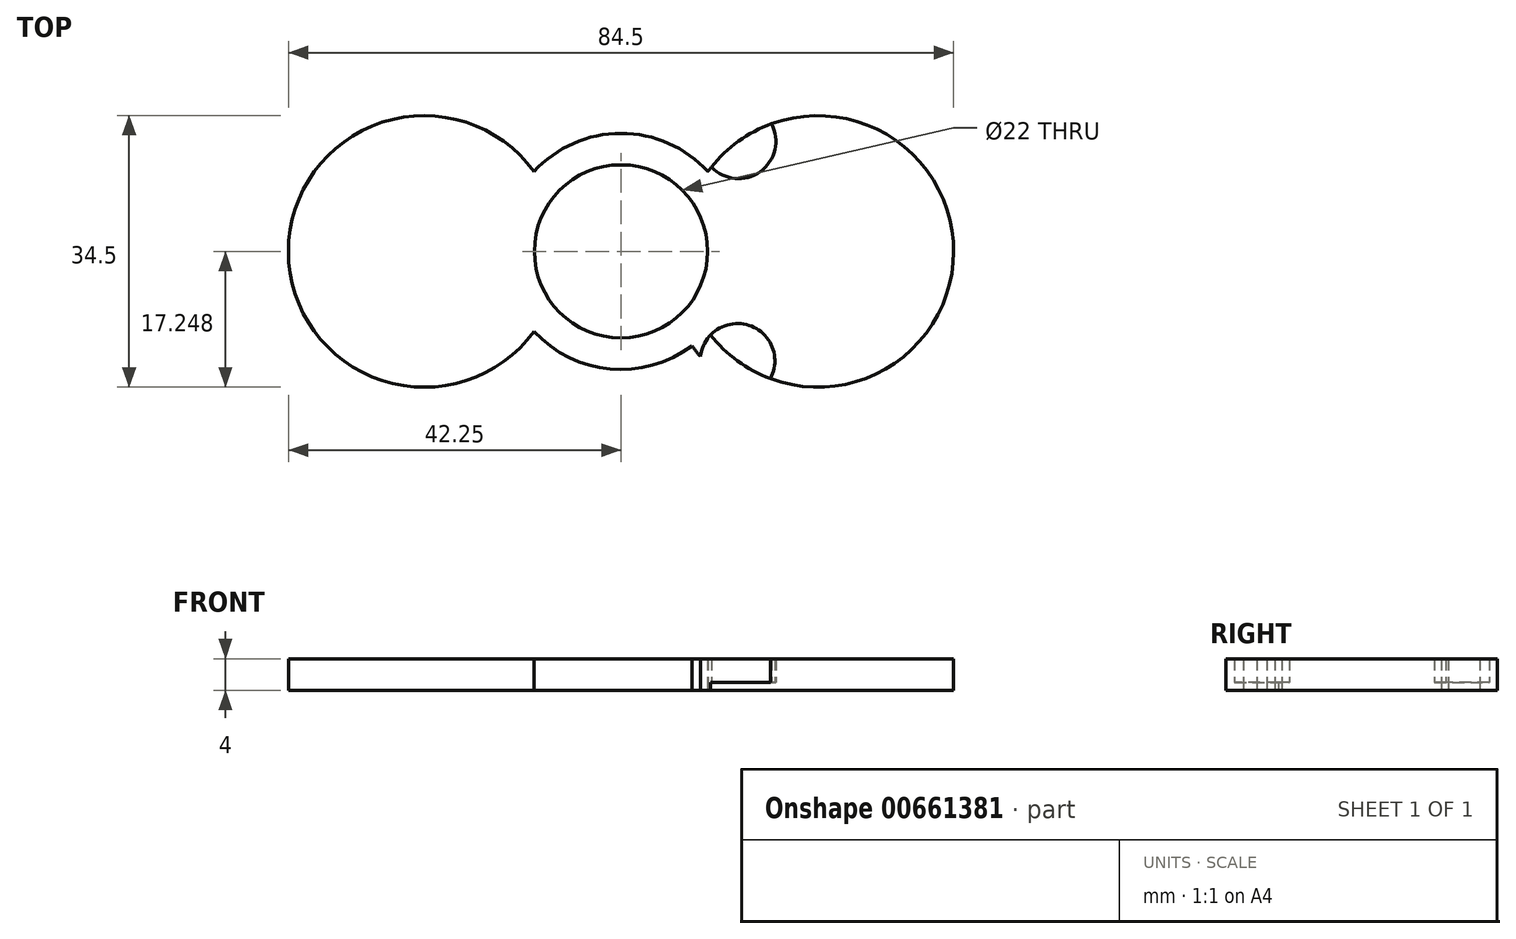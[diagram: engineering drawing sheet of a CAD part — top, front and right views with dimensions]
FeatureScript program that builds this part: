
annotation { "Feature Type Name" : "Feature", "Feature Type Description" : "" }
export const myFeature = defineFeature(function(context is Context, id is Id, definition is map)
    precondition{}
    {
        {
            var Q0;
            Q0=qCreatedBy(makeId("Top.planeOp"),FACE);
            var sketch = newSketch(context, id + "F0", { "sketchPlane" : qUnion([Q0])});
            skCircle(sketch, "E0", {"center": v(25, 38.23) * mm, "radius": 11 * mm});
            skCircle(sketch, "E1", {"center": v(25, 38.23) * mm, "radius": 15 * mm});
            skArc(sketch, "E2", {"start": v(16, 26.23) * mm, "mid": v(-11.02, 54.92) * mm, "end": v(4.76, 18.8) * mm});
            skArc(sketch, "E3", {"start": v(4.5, 57.72) * mm, "mid": v(25, 54.23) * mm, "end": v(45.5, 57.72) * mm});
            skPoint(sketch, "E4", {"position": v(4.5, 18.74) * mm});
            skPoint(sketch, "E5", {"position": v(45.5, 18.74) * mm});
            skArc(sketch, "E6", {"start": v(45.5, 18.74) * mm, "mid": v(40.9, 20.15) * mm, "end": v(36.2, 21.2) * mm});
            skCircle(sketch, "E7", {"center": v(0, 38.23) * mm, "radius": 17.25 * mm});
            skLineSegment(sketch, "E8.anchor1", {"start": v(0, 38.23) * mm, "end": v(0, 23.73) * mm, "construction": true});
            skPoint(sketch, "E9", {"position": v(50, 38.23) * mm});
            skCircle(sketch, "E10", {"center": v(50, 38.23) * mm, "radius": 20 * mm});
            skCircle(sketch, "E11", {"center": v(50, 38.23) * mm, "radius": 17.25 * mm});
            skCircle(sketch, "E12", {"center": v(0, 38.23) * mm, "radius": 7.75 * mm});
            skLineSegment(sketch, "E13", {"start": v(0, 38.23) * mm, "end": v(0, 45.98) * mm});
            skLineSegment(sketch, "E14", {"start": v(0, 45.98) * mm, "end": v(0, 50.73) * mm});
            skLineSegment(sketch, "E15.anchor1", {"start": v(0, 38.23) * mm, "end": v(0, 50.73) * mm, "construction": true});
            skLineSegment(sketch, "E15.anchor2", {"start": v(0, 38.23) * mm, "end": v(0, 25.73) * mm, "construction": true});
            skCircle(sketch, "E16", {"center": v(50, 38.23) * mm, "radius": 7.75 * mm});
            skLineSegment(sketch, "E17", {"start": v(50, 38.23) * mm, "end": v(50, 45.98) * mm});
            skLineSegment(sketch, "E18", {"start": v(50, 45.98) * mm, "end": v(50, 50.73) * mm});
            skCircle(sketch, "E19.1.0", {"center": v(39.92, 52.23) * mm, "radius": 4.75 * mm});
            skCircle(sketch, "E19.4.0", {"center": v(39.8, 24.32) * mm, "radius": 4.75 * mm});
            skLineSegment(sketch, "E19.anchor1", {"start": v(50, 38.23) * mm, "end": v(50, 50.73) * mm, "construction": true});
            skLineSegment(sketch, "E19.anchor2", {"start": v(50, 38.23) * mm, "end": v(50, 25.73) * mm, "construction": true});
            skPoint(sketch, "E20", {"position": v(4.76, 18.8) * mm});
            skSolve(sketch);
        }
        {
            var Q0;
            {var subQ1=sQuery(id+"F0.wireOp",EDGE,"E2");var subQ6=sQuery(id+"F0.wireOp",EDGE,"E1");var subQ7=makeQuery(id+"F0.imprint","INTERSECT",VERTEX,{"disambiguationData":[OD(0.0)],"derivedFrom":[subQ6,subQ1]});Q0=makeQuery(id+"F0.imprint","IMPRINT",FACE,{"disambiguationData":[TD([[makeQuery(id+"F0.imprint","IMPRINT",EDGE,{"disambiguationData":[TD([[subQ7,-1.0]])],"derivedFrom":subQ6}),-1.0]])]});}
            var Q1;
            {var subQ0=sQuery(id+"F0.wireOp",EDGE,"E12");var subQ1=makeQuery(id+"F0.imprint","IMPRINT",VERTEX,{"derivedFrom":subQ0});Q1=makeQuery(id+"F0.imprint","IMPRINT",FACE,{"disambiguationData":[TD([[makeQuery(id+"F0.imprint","IMPRINT",EDGE,{"disambiguationData":[TD([[subQ1,1.0]])],"derivedFrom":subQ0}),1.0]])]});}
            var Q2;
            {var subQ5=sQuery(id+"F0.wireOp",EDGE,"E7");var subQ6=sQuery(id+"F0.wireOp",EDGE,"E1");var subQ9=makeQuery(id+"F0.imprint","INTERSECT",VERTEX,{"disambiguationData":[OD(0.0)],"derivedFrom":[subQ6,subQ5]});Q2=makeQuery(id+"F0.imprint","IMPRINT",FACE,{"disambiguationData":[TD([[makeQuery(id+"F0.imprint","IMPRINT",EDGE,{"disambiguationData":[TD([[subQ9,-1.0]])],"derivedFrom":subQ6}),-1.0]])]});}
            var Q3;
            {var subQ0=sQuery(id+"F0.wireOp",EDGE,"E7");var subQ1=sQuery(id+"F0.wireOp",EDGE,"E0");var subQ2=makeQuery(id+"F0.imprint","INTERSECT",VERTEX,{"disambiguationData":[OD(0.0)],"derivedFrom":[subQ1,subQ0]});Q3=makeQuery(id+"F0.imprint","IMPRINT",FACE,{"disambiguationData":[TD([[makeQuery(id+"F0.imprint","IMPRINT",EDGE,{"disambiguationData":[TD([[subQ2,-1.0]])],"derivedFrom":subQ1}),-1.0]])]});}
            var Q4;
            {var subQ0=sQuery(id+"F0.wireOp",EDGE,"E2");var subQ1=sQuery(id+"F0.wireOp",EDGE,"E0");var subQ2=makeQuery(id+"F0.imprint","INTERSECT",VERTEX,{"disambiguationData":[OD(0.0)],"derivedFrom":[subQ1,subQ0]});Q4=makeQuery(id+"F0.imprint","IMPRINT",FACE,{"disambiguationData":[TD([[makeQuery(id+"F0.imprint","IMPRINT",EDGE,{"disambiguationData":[TD([[subQ2,-1.0]])],"derivedFrom":subQ1}),-1.0]])]});}
            var Q5;
            {var subQ0=sQuery(id+"F0.wireOp",EDGE,"E10");var subQ1=sQuery(id+"F0.wireOp",EDGE,"E0");var subQ2=makeQuery(id+"F0.imprint","INTERSECT",VERTEX,{"disambiguationData":[OD(0.0)],"derivedFrom":[subQ1,subQ0]});Q5=makeQuery(id+"F0.imprint","IMPRINT",FACE,{"disambiguationData":[TD([[makeQuery(id+"F0.imprint","IMPRINT",EDGE,{"disambiguationData":[TD([[subQ2,-1.0]])],"derivedFrom":subQ1}),-1.0]])]});}
            var Q6;
            {var subQ0=sQuery(id+"F0.wireOp",EDGE,"E10");var subQ1=sQuery(id+"F0.wireOp",EDGE,"E0");var subQ2=makeQuery(id+"F0.imprint","INTERSECT",VERTEX,{"disambiguationData":[OD(0.0)],"derivedFrom":[subQ1,subQ0]});Q6=makeQuery(id+"F0.imprint","IMPRINT",FACE,{"disambiguationData":[TD([[makeQuery(id+"F0.imprint","IMPRINT",EDGE,{"disambiguationData":[TD([[subQ2,1.0]])],"derivedFrom":subQ1}),-1.0]])]});}
            var Q7;
            {var subQ0=sQuery(id+"F0.wireOp",EDGE,"E11");var subQ1=sQuery(id+"F0.wireOp",EDGE,"E0");var subQ2=makeQuery(id+"F0.imprint","INTERSECT",VERTEX,{"disambiguationData":[OD(0.0)],"derivedFrom":[subQ1,subQ0]});Q7=makeQuery(id+"F0.imprint","IMPRINT",FACE,{"disambiguationData":[TD([[makeQuery(id+"F0.imprint","IMPRINT",EDGE,{"disambiguationData":[TD([[subQ2,1.0]])],"derivedFrom":subQ1}),-1.0]])]});}
            var Q8;
            {var subQ0=sQuery(id+"F0.wireOp",EDGE,"E10");var subQ1=sQuery(id+"F0.wireOp",EDGE,"E0");var subQ2=makeQuery(id+"F0.imprint","INTERSECT",VERTEX,{"disambiguationData":[OD(1.0)],"derivedFrom":[subQ1,subQ0]});Q8=makeQuery(id+"F0.imprint","IMPRINT",FACE,{"disambiguationData":[TD([[makeQuery(id+"F0.imprint","IMPRINT",EDGE,{"disambiguationData":[TD([[subQ2,-1.0]])],"derivedFrom":subQ1}),-1.0]])]});}
            var Q9;
            {var subQ0=sQuery(id+"F0.wireOp",EDGE,"E2");var subQ1=sQuery(id+"F0.wireOp",EDGE,"E0");var subQ2=makeQuery(id+"F0.imprint","INTERSECT",VERTEX,{"disambiguationData":[OD(1.0)],"derivedFrom":[subQ1,subQ0]});Q9=makeQuery(id+"F0.imprint","IMPRINT",FACE,{"disambiguationData":[TD([[makeQuery(id+"F0.imprint","IMPRINT",EDGE,{"disambiguationData":[TD([[subQ2,-1.0]])],"derivedFrom":subQ1}),-1.0]])]});}
            var Q10;
            {var subQ0=sQuery(id+"F0.wireOp",EDGE,"E2");var subQ1=sQuery(id+"F0.wireOp",EDGE,"E1");var subQ2=makeQuery(id+"F0.imprint","INTERSECT",VERTEX,{"disambiguationData":[OD(1.0)],"derivedFrom":[subQ1,subQ0]});Q10=makeQuery(id+"F0.imprint","IMPRINT",FACE,{"disambiguationData":[TD([[makeQuery(id+"F0.imprint","IMPRINT",EDGE,{"disambiguationData":[TD([[subQ2,-1.0]])],"derivedFrom":subQ1}),-1.0]])]});}
            var Q11;
            {var subQ0=sQuery(id+"F0.wireOp",EDGE,"E10");var subQ1=sQuery(id+"F0.wireOp",EDGE,"E1");var subQ2=makeQuery(id+"F0.imprint","INTERSECT",VERTEX,{"disambiguationData":[OD(0.0)],"derivedFrom":[subQ1,subQ0]});Q11=makeQuery(id+"F0.imprint","IMPRINT",FACE,{"disambiguationData":[TD([[makeQuery(id+"F0.imprint","IMPRINT",EDGE,{"disambiguationData":[TD([[subQ2,-1.0]])],"derivedFrom":subQ1}),-1.0]])]});}
            var Q12;
            {var subQ0=sQuery(id+"F0.wireOp",EDGE,"E7");var subQ1=sQuery(id+"F0.wireOp",EDGE,"E0");var subQ2=makeQuery(id+"F0.imprint","INTERSECT",VERTEX,{"disambiguationData":[OD(1.0)],"derivedFrom":[subQ1,subQ0]});Q12=makeQuery(id+"F0.imprint","IMPRINT",FACE,{"disambiguationData":[TD([[makeQuery(id+"F0.imprint","IMPRINT",EDGE,{"disambiguationData":[TD([[subQ2,-1.0]])],"derivedFrom":subQ1}),-1.0]])]});}
            var Q13;
            {var subQ0=sQuery(id+"F0.wireOp",EDGE,"E10");var subQ10=sQuery(id+"F0.wireOp",EDGE,"E1");var subQ11=makeQuery(id+"F0.imprint","INTERSECT",VERTEX,{"disambiguationData":[OD(0.0)],"derivedFrom":[subQ10,subQ0]});Q13=makeQuery(id+"F0.imprint","IMPRINT",FACE,{"disambiguationData":[TD([[makeQuery(id+"F0.imprint","IMPRINT",EDGE,{"disambiguationData":[TD([[subQ11,1.0]])],"derivedFrom":subQ10}),-1.0]])]});}
            var Q14;
            {var subQ5=sQuery(id+"F0.wireOp",EDGE,"E11");var subQ6=sQuery(id+"F0.wireOp",EDGE,"E1");var subQ9=makeQuery(id+"F0.imprint","INTERSECT",VERTEX,{"disambiguationData":[OD(0.0)],"derivedFrom":[subQ6,subQ5]});Q14=makeQuery(id+"F0.imprint","IMPRINT",FACE,{"disambiguationData":[TD([[makeQuery(id+"F0.imprint","IMPRINT",EDGE,{"disambiguationData":[TD([[subQ9,1.0]])],"derivedFrom":subQ6}),-1.0]])]});}
            var Q15;
            {var subQ0=sQuery(id+"F0.wireOp",EDGE,"E16");var subQ1=makeQuery(id+"F0.imprint","IMPRINT",VERTEX,{"derivedFrom":subQ0});Q15=makeQuery(id+"F0.imprint","IMPRINT",FACE,{"disambiguationData":[TD([[makeQuery(id+"F0.imprint","IMPRINT",EDGE,{"disambiguationData":[TD([[subQ1,-1.0]])],"derivedFrom":subQ0}),1.0]])]});}
            extrude(context, id + "F1", {"entities" : qUnion([Q0, Q1, Q2, Q3, Q4, Q5, Q6, Q7, Q8, Q9, Q10, Q11, Q12, Q13, Q14, Q15]), "depth" : 4 * mm, "offsetDistance" : 25 * mm});
        }
        {
            var Q0;
            {var subQ0=sQuery(id+"F0.wireOp",EDGE,"E15.1.0");var subQ1=makeQuery(id+"F0.imprint","INTERSECT",VERTEX,{"derivedFrom":[sQuery(id+"F0.wireOp",EDGE,"E7"),subQ0]});Q0=makeQuery(id+"F0.imprint","IMPRINT",FACE,{"disambiguationData":[TD([[makeQuery(id+"F0.imprint","IMPRINT",EDGE,{"disambiguationData":[TD([[subQ1,-1.0]])],"derivedFrom":subQ0}),1.0]])]});}
            var Q1;
            {var subQ3=sQuery(id+"F0.wireOp",EDGE,"E12");var subQ5=makeQuery(id+"F0.imprint","IMPRINT",VERTEX,{"derivedFrom":subQ3});Q1=makeQuery(id+"F0.imprint","IMPRINT",FACE,{"disambiguationData":[TD([[makeQuery(id+"F0.imprint","IMPRINT",EDGE,{"disambiguationData":[TD([[subQ5,1.0]])],"derivedFrom":subQ3}),-1.0]])]});}
            var Q2;
            {var subQ0=sQuery(id+"F0.wireOp",EDGE,"E15.4.0");var subQ1=makeQuery(id+"F0.imprint","INTERSECT",VERTEX,{"derivedFrom":[sQuery(id+"F0.wireOp",EDGE,"E7"),subQ0]});Q2=makeQuery(id+"F0.imprint","IMPRINT",FACE,{"disambiguationData":[TD([[makeQuery(id+"F0.imprint","IMPRINT",EDGE,{"disambiguationData":[TD([[subQ1,-1.0]])],"derivedFrom":subQ0}),1.0]])]});}
            var Q3;
            {var subQ0=sQuery(id+"F0.wireOp",EDGE,"E19.1.0");var subQ1=makeQuery(id+"F0.imprint","INTERSECT",VERTEX,{"derivedFrom":[sQuery(id+"F0.wireOp",EDGE,"E11"),subQ0]});Q3=makeQuery(id+"F0.imprint","IMPRINT",FACE,{"disambiguationData":[TD([[makeQuery(id+"F0.imprint","IMPRINT",EDGE,{"disambiguationData":[TD([[subQ1,-1.0]])],"derivedFrom":subQ0}),1.0]])]});}
            var Q4;
            {var subQ3=sQuery(id+"F0.wireOp",EDGE,"E16");var subQ5=makeQuery(id+"F0.imprint","IMPRINT",VERTEX,{"derivedFrom":subQ3});Q4=makeQuery(id+"F0.imprint","IMPRINT",FACE,{"disambiguationData":[TD([[makeQuery(id+"F0.imprint","IMPRINT",EDGE,{"disambiguationData":[TD([[subQ5,-1.0]])],"derivedFrom":subQ3}),-1.0]])]});}
            var Q5;
            {var subQ0=sQuery(id+"F0.wireOp",EDGE,"E19.4.0");var subQ1=makeQuery(id+"F0.imprint","INTERSECT",VERTEX,{"derivedFrom":[sQuery(id+"F0.wireOp",EDGE,"E11"),subQ0]});Q5=makeQuery(id+"F0.imprint","IMPRINT",FACE,{"disambiguationData":[TD([[makeQuery(id+"F0.imprint","IMPRINT",EDGE,{"disambiguationData":[TD([[subQ1,-1.0]])],"derivedFrom":subQ0}),1.0]])]});}
            extrude(context, id + "F2", {"entities" : qUnion([Q0, Q1, Q2, Q3, Q4, Q5]), "operationType" : NewBodyOperationType.ADD, "depth" : 1 * mm, "offsetDistance" : 25 * mm});
        }
    });
